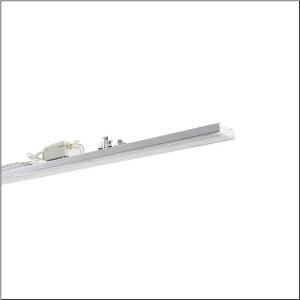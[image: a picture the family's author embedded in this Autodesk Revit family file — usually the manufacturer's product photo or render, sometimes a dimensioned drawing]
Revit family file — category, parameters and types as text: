
# Revit family: licross_r__21_recessed_mo_52te12dv4fxgd_6a3b
name_source: partatom
category: Lighting Fixtures
units: mm (PartAtom-declared; Revit-internal decimal feet)

## family parameters
Cut with Voids When Loaded = No
Host = Face
Light Source = No
Part Type = Normal
Room Calculation Point = No
Round Connector Dimension = Use Diameter
Shared = No

## types (1)
- --- (1 x LED, 15420 lm, 85.3 W, 4000K)
    Apparent Load = 85 VA
    CIE Flux Codes = 72 92 99 100 100
    Color Rendering = 80
    Color Temperature = 4000K
    Default Elevation = 1800 mm
    Description = Licross® 21 Recessed MO, luminaire insert, of sheet steel, galvanised, coil coated, white, length: 2.250mm, width: 66mm, height: 67mm, LED rated luminous flux: 15.420lm, light colour: 840, control gear: DALI 2, with plug, 6-pole, with phase selection, mains connection: 220..240V, AC/DC, 0/50..60Hz, rated input power: 85W, without changeover relay, for emergency light function, for central battery installations according to DIN EN 60598-2-22, halogen-free wiring, primary optical cover: cover, of PMMA, light emission: direct distribution, primary light characteristic: symmetric, protection rating (complete): IP54, insulation class (complete): insulation class I (protective earthing), certification: CE, ENEC, VDE, UKCA, protection symbol: D if used in an environment with non-conductive dust loads with corresponding accessories, impact resistance: IK06, permissible ambient temperature for indoor applications: -25..+35°C, standard: EN 60598-2-22, corresponds to IFS (International Featured Standards) requirements for safety and quality in the food industry, reducing of maximum allowable ambient temperature of 5°C with ceiling mounting, LABS conformity tested according to VDMA 24364:2018-05, packaging unit: 1 piece
    Height = 58 mm
    Lamp = 1 x LED
    Lamp Light Flux = 15420 lm
    Lamp Power = 85.3 W
    Lamp count = 1
    Length = 2250 mm
    Luminous efficacy = 181 lm/W
    Manufacturer = Siteco
    ModVariant = No
    Model = 52TE12DV4FXGD
    Mounting Place = Ceiling
    Mounting Type = Pendant
    Number of Poles = 1
    OnlyDefault = Yes
    Power Factor = 1
    Product Name = Licross® 21 Recessed MO
    Product group = luminaire insert
    ProductGroupID = 901
    Protection Class = Protection class I
    Protection Degree = IP 54
    RLX_Detail_Level = 1
    RLX_Emergency_Light_Flux = 0 lm
    RLX_Emergency_Type = 0
    RLX_Emergency_Type_DB = No
    RlxData = <blob elided: 30001 chars, md5=75c4b144>
    Socket = socket
    Standby Power = 0 W
    System Light Flux = 15420 lm
    System Power = 85 W
    Type Comments = : AC-mode, luminous flux: 100 % | dim-lin: 254 | 390 mA
    Type Image = l_1296930.jpg
    URL = http://relux.com
    VarID = @adj_043101
    Voltage = 0 V
    Weight = 0.00 kg
    Width = 66 mm

## geometry (parser evidence)
native form markers: Blend x4, Sweep x11
no freeform markers — native parametric forms only
